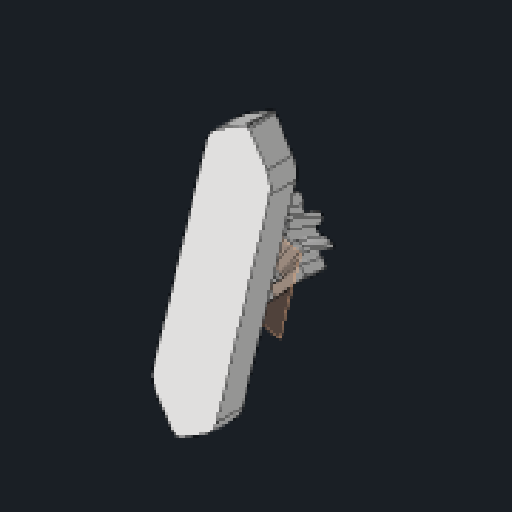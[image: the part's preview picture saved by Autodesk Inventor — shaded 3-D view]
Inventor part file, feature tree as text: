
AUTODESK INVENTOR PART (.ipt)
format: ipt  version: 2023.2 (Build 272271030, 271C)  size: 1,459,200 bytes
history: native  units: mm
features: sketch x3, extrude x3, plane x2, fillet x2, projected_geometry x2, helix x1, pattern_circular x1, mirror x1, chamfer x1
ambient origin geometry x8: Origin, YZ Plane, XZ Plane, XY Plane, X Axis, Y Axis, Z Axis, Center Point
bodies: Solid1 (feature_tree)
feature tree (16):
  sketch  "Sketch1"  dims[d0=5.0mm d1=0.0mm]
  extrude  "Extrusion1"  Depth=10.0mm TaperAngle=360.0deg
  helix  "Coil1"  [1 undecoded]
  pattern_circular  "Circular Pattern1"  Count=3  [1 undecoded]
  mirror  "Mirror1"
  plane  "Work Plane2"
  plane  "Work Plane1"
  extrude  "Extrusion2"  Depth=5.0mm TaperAngle=0.0deg
  extrude  "Extrusion3"  Depth=5.0mm TaperAngle=0.0deg
  chamfer  "Chamfer1"  Distance=0.5mm
  fillet  "Fillet2"  Radius=5.0mm
  fillet  "Fillet3"  [1 undecoded]
  sketch  "Sketch3"  dims[d2=100.0mm d3=10.0mm d4=10.0mm d5=0.0mm d6=90.0deg d7=90.0deg d8=0.0mm d9=0.0mm d10=80.0mm d11=360.0deg d13=6.75mm]
  projected_geometry  "Projected Loop1"
  sketch  "Sketch4"  dims[d15=2.0mm d16=0.0mm d17=30.0mm d18=5.0mm d19=0.0mm d21=0.0mm d22=6.0mm d23=2.0mm d24=45.0deg d25=0.5mm d26=5.0mm]
  projected_geometry  "Projected Loop2"
note: 3 required parameter values undecoded (feature->parameter linkage not recoverable at this tier; creation-order binding heuristic only, values carry confidence <= 0.55)
